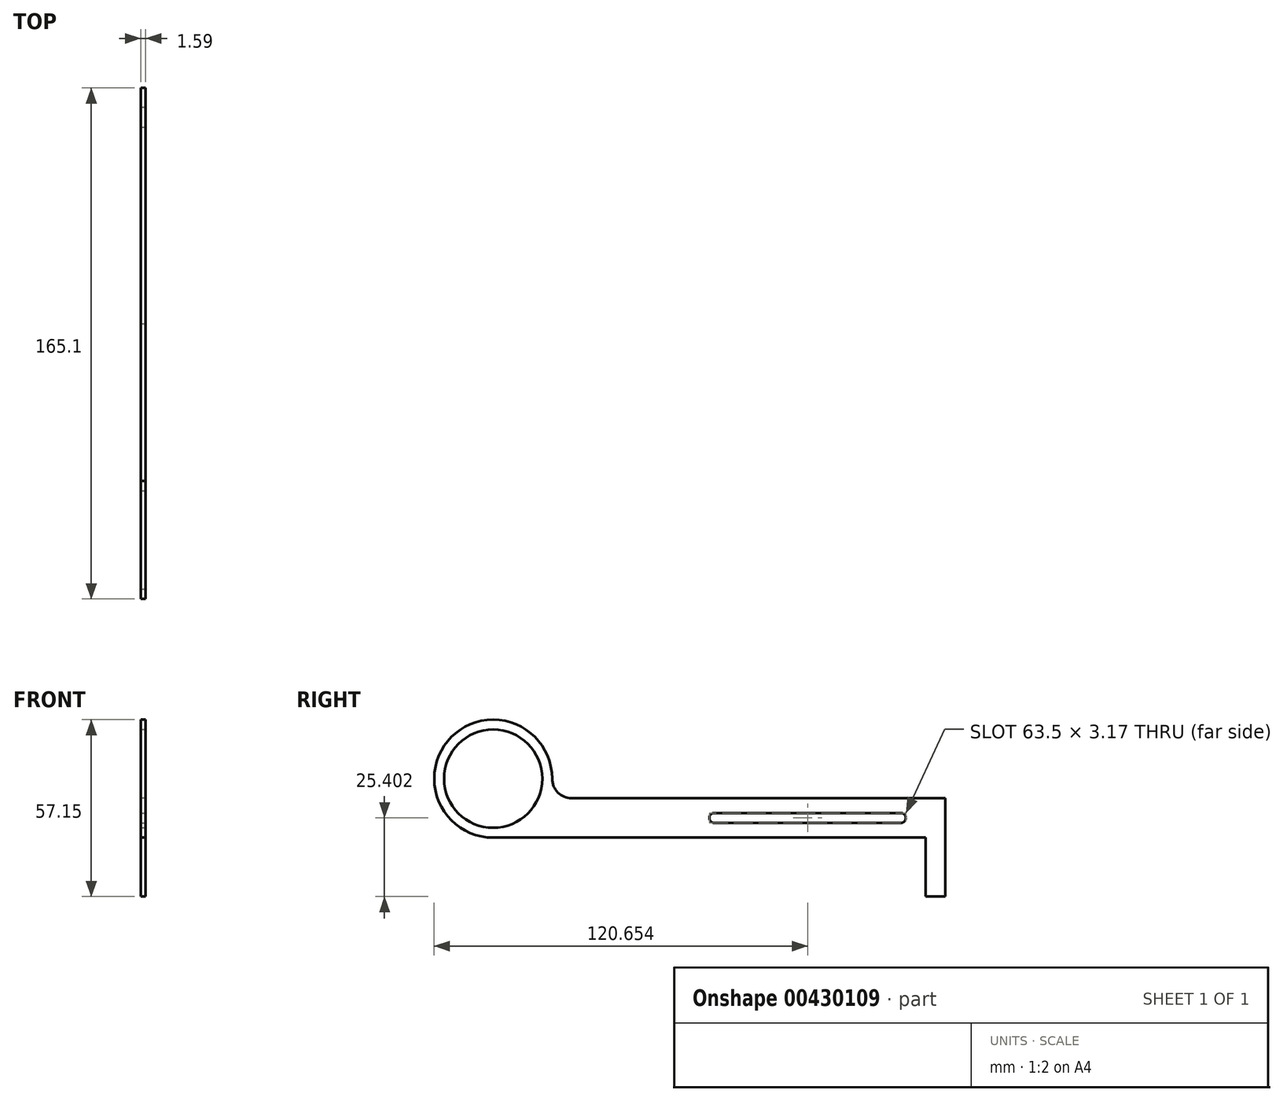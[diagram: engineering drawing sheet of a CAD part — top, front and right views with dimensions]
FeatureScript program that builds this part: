
annotation { "Feature Type Name" : "Feature", "Feature Type Description" : "" }
export const myFeature = defineFeature(function(context is Context, id is Id, definition is map)
    precondition{}
    {
        {
            var Q0;
            Q0=qCreatedBy(makeId("Right.planeOp"),FACE);
            var sketch = newSketch(context, id + "F0", { "sketchPlane" : qUnion([Q0])});
            skLineSegment(sketch, "E0", {"start": v(-101.24, 43.53) * mm, "end": v(-63.14, 43.53) * mm});
            skLineSegment(sketch, "E1", {"start": v(-63.14, 43.53) * mm, "end": v(-63.14, 18.13) * mm});
            skLineSegment(sketch, "E2", {"start": v(-63.14, 18.13) * mm, "end": v(63.86, 18.13) * mm});
            skLineSegment(sketch, "E3", {"start": v(63.86, 18.13) * mm, "end": v(63.86, -13.62) * mm});
            skLineSegment(sketch, "E4", {"start": v(63.86, -13.62) * mm, "end": v(57.51, -13.62) * mm});
            skLineSegment(sketch, "E5", {"start": v(57.51, -13.62) * mm, "end": v(57.51, 5.43) * mm});
            skLineSegment(sketch, "E6", {"start": v(57.51, 5.43) * mm, "end": v(-101.24, 5.43) * mm});
            skLineSegment(sketch, "E7", {"start": v(-101.24, 5.43) * mm, "end": v(-101.24, 43.53) * mm});
            skSolve(sketch);
        }
        {
            var Q0;
            Q0 = qSketchRegion(id + "F0", true);
            extrude(context, id + "F1", {"entities" : qUnion([Q0]), "depth" : 1.59 * mm});
        }
        {
            var Q0;
            Q0=makeQuery(id+"F1.opExtrude","SWEPT_EDGE",EDGE,{"disambiguationData":[OSD([sQuery(id+"F0.wireOp",EDGE,"E0"),sQuery(id+"F0.wireOp",EDGE,"E1")])]});
            var Q1;
            Q1=makeQuery(id+"F1.opExtrude","SWEPT_EDGE",EDGE,{"disambiguationData":[OSD([sQuery(id+"F0.wireOp",EDGE,"E0"),sQuery(id+"F0.wireOp",EDGE,"E7")])]});
            var Q2;
            Q2=makeQuery(id+"F1.opExtrude","SWEPT_EDGE",EDGE,{"disambiguationData":[OSD([sQuery(id+"F0.wireOp",EDGE,"E6"),sQuery(id+"F0.wireOp",EDGE,"E7")])]});
            fillet(context, id + "F2", {"entities" : qUnion([Q0, Q1, Q2]), "radius" : 19.05 * mm, "tangentPropagation" : true, "allowEdgeOverflow" : false});
        }
        {
            var Q0;
            Q0=makeQuery(id+"F1.opExtrude","SWEPT_EDGE",EDGE,{"disambiguationData":[OSD([sQuery(id+"F0.wireOp",EDGE,"E1"),sQuery(id+"F0.wireOp",EDGE,"E2")])]});
            fillet(context, id + "F3", {"entities" : qUnion([Q0]), "radius" : 6.35 * mm, "tangentPropagation" : true, "allowEdgeOverflow" : false});
        }
        {
            var Q0;
            Q0=makeQuery(id+"F1.opExtrude","CAP_FACE",FACE,{"disambiguationData":[OSD([sQuery(id+"F0.wireOp",EDGE,"E0"),sQuery(id+"F0.wireOp",EDGE,"E1"),sQuery(id+"F0.wireOp",EDGE,"E2"),sQuery(id+"F0.wireOp",EDGE,"E3"),sQuery(id+"F0.wireOp",EDGE,"E4"),sQuery(id+"F0.wireOp",EDGE,"E5"),sQuery(id+"F0.wireOp",EDGE,"E6"),sQuery(id+"F0.wireOp",EDGE,"E7")])],"isStart":false});
            var sketch = newSketch(context, id + "F4", { "sketchPlane" : qUnion([Q0])});
            skCircle(sketch, "E8", {"center": v(-82.19, 24.48) * mm, "radius": 15.88 * mm});
            skSolve(sketch);
        }
        {
            var Q0;
            Q0 = qSketchRegion(id + "F4", true);
            extrude(context, id + "F5", {"entities" : qUnion([Q0]), "operationType" : NewBodyOperationType.REMOVE, "oppositeDirection" : true, "depth" : 25.4 * mm});
        }
        {
            var Q0;
            Q0=makeQuery(id+"F1.opExtrude","CAP_FACE",FACE,{"disambiguationData":[OSD([sQuery(id+"F0.wireOp",EDGE,"E0"),sQuery(id+"F0.wireOp",EDGE,"E1"),sQuery(id+"F0.wireOp",EDGE,"E2"),sQuery(id+"F0.wireOp",EDGE,"E3"),sQuery(id+"F0.wireOp",EDGE,"E4"),sQuery(id+"F0.wireOp",EDGE,"E5"),sQuery(id+"F0.wireOp",EDGE,"E6"),sQuery(id+"F0.wireOp",EDGE,"E7")])],"isStart":false});
            var sketch = newSketch(context, id + "F6", { "sketchPlane" : qUnion([Q0])});
            skLineSegment(sketch, "E9.bottom", {"start": v(-12.34, 13.37) * mm, "end": v(51.16, 13.37) * mm});
            skLineSegment(sketch, "E9.top", {"start": v(-12.34, 10.2) * mm, "end": v(51.16, 10.2) * mm});
            skLineSegment(sketch, "E9.left", {"start": v(-12.34, 13.37) * mm, "end": v(-12.34, 10.2) * mm});
            skLineSegment(sketch, "E9.right", {"start": v(51.16, 13.37) * mm, "end": v(51.16, 10.2) * mm});
            skSolve(sketch);
        }
        {
            var Q0;
            Q0 = qSketchRegion(id + "F6", true);
            extrude(context, id + "F7", {"entities" : qUnion([Q0]), "operationType" : NewBodyOperationType.REMOVE, "oppositeDirection" : true, "depth" : 25.4 * mm});
        }
        {
            var Q0;
            Q0=makeQuery(id+"F7.boolean.opBoolean","COPY",EDGE,{"derivedFrom":makeQuery(id+"F7.opExtrude","SWEPT_EDGE",EDGE,{"disambiguationData":[OSD([sQuery(id+"F6.wireOp",EDGE,"E9.bottom"),sQuery(id+"F6.wireOp",EDGE,"E9.left")])]})});
            var Q1;
            Q1=makeQuery(id+"F7.boolean.opBoolean","COPY",EDGE,{"derivedFrom":makeQuery(id+"F7.opExtrude","SWEPT_EDGE",EDGE,{"disambiguationData":[OSD([sQuery(id+"F6.wireOp",EDGE,"E9.top"),sQuery(id+"F6.wireOp",EDGE,"E9.left")])]})});
            var Q2;
            Q2=makeQuery(id+"F7.boolean.opBoolean","COPY",EDGE,{"derivedFrom":makeQuery(id+"F7.opExtrude","SWEPT_EDGE",EDGE,{"disambiguationData":[OSD([sQuery(id+"F6.wireOp",EDGE,"E9.top"),sQuery(id+"F6.wireOp",EDGE,"E9.right")])]})});
            var Q3;
            Q3=makeQuery(id+"F7.boolean.opBoolean","COPY",EDGE,{"derivedFrom":makeQuery(id+"F7.opExtrude","SWEPT_EDGE",EDGE,{"disambiguationData":[OSD([sQuery(id+"F6.wireOp",EDGE,"E9.bottom"),sQuery(id+"F6.wireOp",EDGE,"E9.right")])]})});
            fillet(context, id + "F8", {"entities" : qUnion([Q0, Q1, Q2, Q3]), "radius" : 1.59 * mm, "tangentPropagation" : true, "allowEdgeOverflow" : false});
        }
    });
